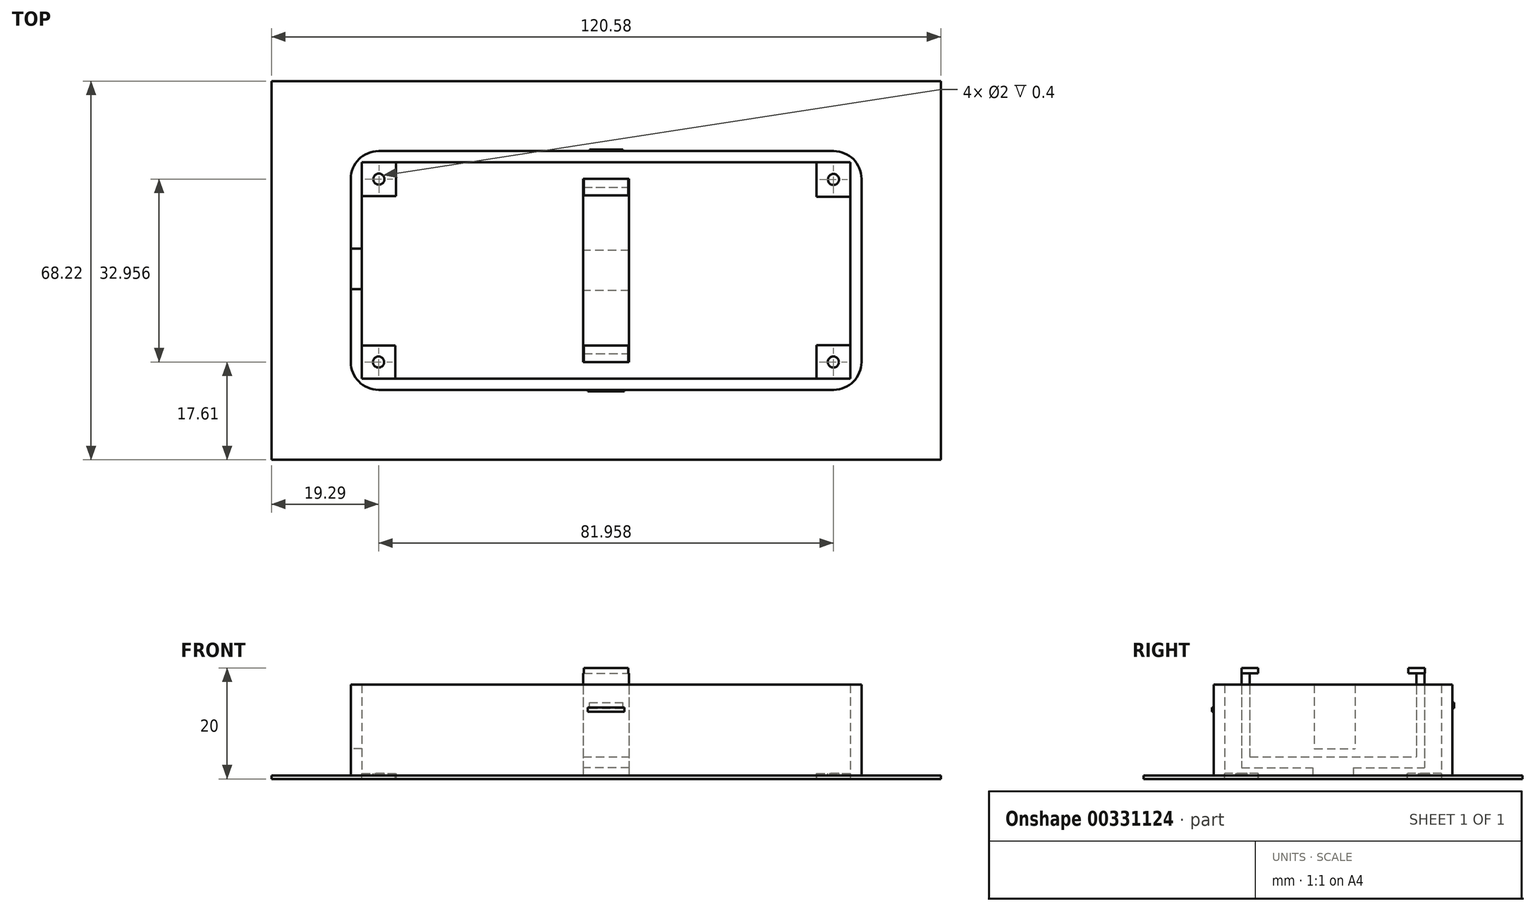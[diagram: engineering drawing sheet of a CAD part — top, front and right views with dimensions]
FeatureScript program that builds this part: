
annotation { "Feature Type Name" : "Feature", "Feature Type Description" : "" }
export const myFeature = defineFeature(function(context is Context, id is Id, definition is map)
    precondition{}
    {
        {
            var Q0;
            Q0=qCreatedBy(makeId("Top.planeOp"),FACE);
            var sketch = newSketch(context, id + "F0", { "sketchPlane" : qUnion([Q0])});
            skLineSegment(sketch, "E0.bottom", {"start": v(-46, 21.5) * mm, "end": v(46, 21.5) * mm});
            skLineSegment(sketch, "E0.top", {"start": v(-46, -21.5) * mm, "end": v(46, -21.5) * mm});
            skLineSegment(sketch, "E0.left", {"start": v(-46, 21.5) * mm, "end": v(-46, -21.5) * mm});
            skLineSegment(sketch, "E0.right", {"start": v(46, 21.5) * mm, "end": v(46, -21.5) * mm});
            skPoint(sketch, "E0.middle", {"position": v(0, 0) * mm});
            skLineSegment(sketch, "E1.bottom", {"start": v(-44, 19.5) * mm, "end": v(44, 19.5) * mm});
            skLineSegment(sketch, "E1.top", {"start": v(-44, -19.5) * mm, "end": v(44, -19.5) * mm});
            skLineSegment(sketch, "E1.left", {"start": v(-44, 19.5) * mm, "end": v(-44, -19.5) * mm});
            skLineSegment(sketch, "E1.right", {"start": v(44, 19.5) * mm, "end": v(44, -19.5) * mm});
            skLineSegment(sketch, "E2.bottom", {"start": v(-4.12, 19.5) * mm, "end": v(4.12, 19.5) * mm});
            skLineSegment(sketch, "E2.top", {"start": v(-4.12, -19.5) * mm, "end": v(4.12, -19.5) * mm});
            skLineSegment(sketch, "E2.left", {"start": v(-4.12, 19.5) * mm, "end": v(-4.12, -19.5) * mm});
            skLineSegment(sketch, "E2.right", {"start": v(4.12, 19.5) * mm, "end": v(4.12, -19.5) * mm});
            skLineSegment(sketch, "E3.bottom", {"start": v(44, 3.63) * mm, "end": v(-44, 3.63) * mm});
            skLineSegment(sketch, "E3.top", {"start": v(44, -3.63) * mm, "end": v(-44, -3.63) * mm});
            skLineSegment(sketch, "E3.left", {"start": v(44, 3.63) * mm, "end": v(44, -3.63) * mm});
            skLineSegment(sketch, "E3.right", {"start": v(-44, 3.63) * mm, "end": v(-44, -3.63) * mm});
            skSolve(sketch);
        }
        {
            var Q0;
            {var subQ5=sQuery(id+"F0.wireOp",EDGE,"E3.right");Q0=makeQuery(id+"F0.imprint","IMPRINT",FACE,{"disambiguationData":[TD([[makeQuery(id+"F0.imprint","IMPRINT",EDGE,{"derivedFrom":subQ5}),1.0]])]});}
            var Q1;
            {var subQ5=sQuery(id+"F0.wireOp",EDGE,"E3.left");Q1=makeQuery(id+"F0.imprint","IMPRINT",FACE,{"disambiguationData":[TD([[makeQuery(id+"F0.imprint","IMPRINT",EDGE,{"derivedFrom":subQ5}),-1.0]])]});}
            var Q2;
            {var subQ0=sQuery(id+"F0.wireOp",EDGE,"E2.top");Q2=makeQuery(id+"F0.imprint","IMPRINT",FACE,{"disambiguationData":[TD([[makeQuery(id+"F0.imprint","IMPRINT",EDGE,{"derivedFrom":subQ0}),1.0]])]});}
            var Q3;
            {var subQ0=sQuery(id+"F0.wireOp",EDGE,"E3.bottom");var subQ1=sQuery(id+"F0.wireOp",EDGE,"E2.left");var subQ2=makeQuery(id+"F0.imprint","INTERSECT",VERTEX,{"derivedFrom":[subQ1,subQ0]});Q3=makeQuery(id+"F0.imprint","IMPRINT",FACE,{"disambiguationData":[TD([[makeQuery(id+"F0.imprint","IMPRINT",EDGE,{"disambiguationData":[TD([[subQ2,-1.0]])],"derivedFrom":subQ1}),1.0]])]});}
            var Q4;
            {var subQ0=sQuery(id+"F0.wireOp",EDGE,"E2.bottom");Q4=makeQuery(id+"F0.imprint","IMPRINT",FACE,{"disambiguationData":[TD([[makeQuery(id+"F0.imprint","IMPRINT",EDGE,{"derivedFrom":subQ0}),-1.0]])]});}
            var Q5;
            Q5=makeQuery(id+"F0.imprint","IMPRINT",FACE,{"disambiguationData":[TD([[makeQuery(id+"F0.imprint","IMPRINT",EDGE,{"derivedFrom":sQuery(id+"F0.wireOp",EDGE,"E0.bottom")}),-1.0]])]});
            extrude(context, id + "F1", {"entities" : qUnion([Q0, Q1, Q2, Q3, Q4, Q5]), "depth" : 2 * mm});
        }
        {
            var Q0;
            Q0=makeQuery(id+"F1.opExtrude","CAP_FACE",FACE,{"disambiguationData":[OSD([sQuery(id+"F0.wireOp",EDGE,"E0.bottom"),sQuery(id+"F0.wireOp",EDGE,"E0.top"),sQuery(id+"F0.wireOp",EDGE,"E0.left"),sQuery(id+"F0.wireOp",EDGE,"E0.right"),sQuery(id+"F0.wireOp",EDGE,"E1.bottom"),sQuery(id+"F0.wireOp",EDGE,"E1.top"),sQuery(id+"F0.wireOp",EDGE,"E1.left"),sQuery(id+"F0.wireOp",EDGE,"E1.right"),sQuery(id+"F0.wireOp",EDGE,"E2.left"),sQuery(id+"F0.wireOp",EDGE,"E2.right"),sQuery(id+"F0.wireOp",EDGE,"E3.bottom"),sQuery(id+"F0.wireOp",EDGE,"E3.top")])],"isStart":false});
            var sketch = newSketch(context, id + "F2", { "sketchPlane" : qUnion([Q0])});
            skLineSegment(sketch, "E4.bottom", {"start": v(-4.12, 15) * mm, "end": v(4.12, 15) * mm});
            skLineSegment(sketch, "E4.top", {"start": v(-4.12, 16.5) * mm, "end": v(4.12, 16.5) * mm});
            skLineSegment(sketch, "E4.left", {"start": v(-4.12, 15) * mm, "end": v(-4.12, 16.5) * mm});
            skLineSegment(sketch, "E4.right", {"start": v(4.12, 15) * mm, "end": v(4.12, 16.5) * mm});
            skPoint(sketch, "E4.middle", {"position": v(0, 15.75) * mm});
            skLineSegment(sketch, "E5.bottom", {"start": v(-4.12, -15) * mm, "end": v(4.12, -15) * mm});
            skLineSegment(sketch, "E5.top", {"start": v(-4.12, -16.5) * mm, "end": v(4.12, -16.5) * mm});
            skLineSegment(sketch, "E5.left", {"start": v(-4.12, -15) * mm, "end": v(-4.12, -16.5) * mm});
            skLineSegment(sketch, "E5.right", {"start": v(4.12, -15) * mm, "end": v(4.12, -16.5) * mm});
            skPoint(sketch, "E5.middle", {"position": v(0, -15.75) * mm});
            skSolve(sketch);
        }
        {
            var Q0;
            Q0=makeQuery(id+"F2.imprint","IMPRINT",FACE,{"disambiguationData":[TD([[makeQuery(id+"F2.imprint","IMPRINT",EDGE,{"derivedFrom":sQuery(id+"F2.wireOp",EDGE,"E4.bottom")}),1.0]])]});
            extrude(context, id + "F3", {"entities" : qUnion([Q0]), "operationType" : NewBodyOperationType.ADD, "depth" : 17 * mm});
        }
        {
            var Q0;
            Q0=makeQuery(id+"F2.imprint","IMPRINT",FACE,{"disambiguationData":[TD([[makeQuery(id+"F2.imprint","IMPRINT",EDGE,{"derivedFrom":sQuery(id+"F2.wireOp",EDGE,"E5.bottom")}),-1.0]])]});
            extrude(context, id + "F4", {"entities" : qUnion([Q0]), "operationType" : NewBodyOperationType.ADD, "depth" : 17 * mm});
        }
        {
            var Q0;
            Q0=makeQuery(id+"F1.opExtrude","CAP_FACE",FACE,{"disambiguationData":[OSD([sQuery(id+"F0.wireOp",EDGE,"E0.bottom"),sQuery(id+"F0.wireOp",EDGE,"E0.top"),sQuery(id+"F0.wireOp",EDGE,"E0.left"),sQuery(id+"F0.wireOp",EDGE,"E0.right"),sQuery(id+"F0.wireOp",EDGE,"E1.bottom"),sQuery(id+"F0.wireOp",EDGE,"E1.top"),sQuery(id+"F0.wireOp",EDGE,"E1.left"),sQuery(id+"F0.wireOp",EDGE,"E1.right"),sQuery(id+"F0.wireOp",EDGE,"E2.left"),sQuery(id+"F0.wireOp",EDGE,"E2.right"),sQuery(id+"F0.wireOp",EDGE,"E3.bottom"),sQuery(id+"F0.wireOp",EDGE,"E3.top")])],"isStart":false});
            var sketch = newSketch(context, id + "F5", { "sketchPlane" : qUnion([Q0])});
            skLineSegment(sketch, "E6.bottom", {"start": v(-4.12, -15) * mm, "end": v(4.12, -15) * mm});
            skLineSegment(sketch, "E6.top", {"start": v(-4.12, 15) * mm, "end": v(4.12, 15) * mm});
            skLineSegment(sketch, "E6.left", {"start": v(-4.12, -15) * mm, "end": v(-4.12, 15) * mm});
            skLineSegment(sketch, "E6.right", {"start": v(4.12, -15) * mm, "end": v(4.12, 15) * mm});
            skPoint(sketch, "E6.middle", {"position": v(0, 0) * mm});
            skSolve(sketch);
        }
        {
            var Q0;
            {var subQ9=sQuery(id+"F5.wireOp",EDGE,"E6.bottom");Q0=makeQuery(id+"F5.imprint","IMPRINT",FACE,{"disambiguationData":[TD([[makeQuery(id+"F5.imprint","IMPRINT",EDGE,{"derivedFrom":subQ9}),1.0]])]});}
            extrude(context, id + "F6", {"entities" : qUnion([Q0]), "operationType" : NewBodyOperationType.ADD, "depth" : 2 * mm});
        }
        {
            var Q0;
            Q0=makeQuery(id+"F4.opExtrude","CAP_FACE",FACE,{"disambiguationData":[OSD([sQuery(id+"F2.wireOp",EDGE,"E5.bottom"),sQuery(id+"F2.wireOp",EDGE,"E5.top"),sQuery(id+"F2.wireOp",EDGE,"E5.left"),sQuery(id+"F2.wireOp",EDGE,"E5.right")])],"isStart":false});
            var sketch = newSketch(context, id + "F7", { "sketchPlane" : qUnion([Q0])});
            skLineSegment(sketch, "E7.bottom", {"start": v(-4, -13.5) * mm, "end": v(4, -13.5) * mm});
            skLineSegment(sketch, "E7.top", {"start": v(-4, -16.5) * mm, "end": v(4, -16.5) * mm});
            skLineSegment(sketch, "E7.left", {"start": v(-4, -13.5) * mm, "end": v(-4, -16.5) * mm});
            skLineSegment(sketch, "E7.right", {"start": v(4, -13.5) * mm, "end": v(4, -16.5) * mm});
            skPoint(sketch, "E7.middle", {"position": v(0, -15) * mm});
            skLineSegment(sketch, "E8.bottom", {"start": v(-4, 13.54) * mm, "end": v(4, 13.54) * mm});
            skLineSegment(sketch, "E8.top", {"start": v(-4, 16.54) * mm, "end": v(4, 16.54) * mm});
            skLineSegment(sketch, "E8.left", {"start": v(-4, 13.54) * mm, "end": v(-4, 16.54) * mm});
            skLineSegment(sketch, "E8.right", {"start": v(4, 13.54) * mm, "end": v(4, 16.54) * mm});
            skPoint(sketch, "E8.middle", {"position": v(0, 15.04) * mm});
            skSolve(sketch);
        }
        {
            var Q0;
            Q0 = qSketchRegion(id + "F7", true);
            extrude(context, id + "F8", {"entities" : qUnion([Q0]), "operationType" : NewBodyOperationType.ADD, "depth" : 1 * mm});
        }
        {
            var Q0;
            Q0=qCreatedBy(makeId("Top.planeOp"),FACE);
            var sketch = newSketch(context, id + "F9", { "sketchPlane" : qUnion([Q0])});
            skLineSegment(sketch, "E9.bottom", {"start": v(-46, -21.5) * mm, "end": v(-38, -21.5) * mm});
            skLineSegment(sketch, "E9.top", {"start": v(-46, -13.5) * mm, "end": v(-38, -13.5) * mm});
            skLineSegment(sketch, "E9.left", {"start": v(-46, -21.5) * mm, "end": v(-46, -13.5) * mm});
            skLineSegment(sketch, "E9.right", {"start": v(-38, -21.5) * mm, "end": v(-38, -13.5) * mm});
            skSolve(sketch);
        }
        {
            var Q0;
            Q0=qCreatedBy(makeId("Top.planeOp"),FACE);
            var sketch = newSketch(context, id + "F10", { "sketchPlane" : qUnion([Q0])});
            skLineSegment(sketch, "E10.bottom", {"start": v(-45.88, 21.41) * mm, "end": v(-37.88, 21.41) * mm});
            skLineSegment(sketch, "E10.top", {"start": v(-45.88, 13.41) * mm, "end": v(-37.88, 13.41) * mm});
            skLineSegment(sketch, "E10.left", {"start": v(-45.88, 21.41) * mm, "end": v(-45.88, 13.41) * mm});
            skLineSegment(sketch, "E10.right", {"start": v(-37.88, 21.41) * mm, "end": v(-37.88, 13.41) * mm});
            skSolve(sketch);
        }
        {
            var Q0;
            Q0 = qSketchRegion(id + "F10", true);
            extrude(context, id + "F11", {"entities" : qUnion([Q0]), "operationType" : NewBodyOperationType.ADD, "depth" : 1 * mm});
        }
        {
            var Q0;
            Q0 = qSketchRegion(id + "F9", true);
            extrude(context, id + "F12", {"entities" : qUnion([Q0]), "operationType" : NewBodyOperationType.ADD, "depth" : 1 * mm});
        }
        {
            var Q0;
            Q0=qCreatedBy(makeId("Top.planeOp"),FACE);
            var sketch = newSketch(context, id + "F13", { "sketchPlane" : qUnion([Q0])});
            skLineSegment(sketch, "E11.bottom", {"start": v(45.92, 21.28) * mm, "end": v(37.92, 21.28) * mm});
            skLineSegment(sketch, "E11.top", {"start": v(45.92, 13.28) * mm, "end": v(37.92, 13.28) * mm});
            skLineSegment(sketch, "E11.left", {"start": v(45.92, 21.28) * mm, "end": v(45.92, 13.28) * mm});
            skLineSegment(sketch, "E11.right", {"start": v(37.92, 21.28) * mm, "end": v(37.92, 13.28) * mm});
            skSolve(sketch);
        }
        {
            var Q0;
            Q0 = qSketchRegion(id + "F13", true);
            extrude(context, id + "F14", {"entities" : qUnion([Q0]), "operationType" : NewBodyOperationType.ADD, "depth" : 1 * mm});
        }
        {
            var Q0;
            Q0=qCreatedBy(makeId("Top.planeOp"),FACE);
            var sketch = newSketch(context, id + "F15", { "sketchPlane" : qUnion([Q0])});
            skLineSegment(sketch, "E12.bottom", {"start": v(45.87, -21.5) * mm, "end": v(37.87, -21.5) * mm});
            skLineSegment(sketch, "E12.top", {"start": v(45.87, -13.5) * mm, "end": v(37.87, -13.5) * mm});
            skLineSegment(sketch, "E12.left", {"start": v(45.87, -21.5) * mm, "end": v(45.87, -13.5) * mm});
            skLineSegment(sketch, "E12.right", {"start": v(37.87, -21.5) * mm, "end": v(37.87, -13.5) * mm});
            skSolve(sketch);
        }
        {
            var Q0;
            Q0 = qSketchRegion(id + "F15", true);
            extrude(context, id + "F16", {"entities" : qUnion([Q0]), "operationType" : NewBodyOperationType.ADD, "depth" : 1 * mm});
        }
        {
            var Q0;
            Q0=makeQuery(id+"F1.opExtrude","CAP_FACE",FACE,{"disambiguationData":[OSD([sQuery(id+"F0.wireOp",EDGE,"E0.bottom"),sQuery(id+"F0.wireOp",EDGE,"E0.top"),sQuery(id+"F0.wireOp",EDGE,"E0.left"),sQuery(id+"F0.wireOp",EDGE,"E0.right"),sQuery(id+"F0.wireOp",EDGE,"E1.bottom"),sQuery(id+"F0.wireOp",EDGE,"E1.top"),sQuery(id+"F0.wireOp",EDGE,"E1.left"),sQuery(id+"F0.wireOp",EDGE,"E1.right"),sQuery(id+"F0.wireOp",EDGE,"E2.left"),sQuery(id+"F0.wireOp",EDGE,"E2.right"),sQuery(id+"F0.wireOp",EDGE,"E3.bottom"),sQuery(id+"F0.wireOp",EDGE,"E3.top")])],"isStart":false});
            var sketch = newSketch(context, id + "F17", { "sketchPlane" : qUnion([Q0])});
            skLineSegment(sketch, "E13", {"start": v(-4.12, -19.5) * mm, "end": v(4.12, -19.5) * mm});
            skLineSegment(sketch, "E14", {"start": v(-4.12, 19.5) * mm, "end": v(4.12, 19.5) * mm});
            skLineSegment(sketch, "E15", {"start": v(44, -3.63) * mm, "end": v(44, 3.63) * mm});
            skLineSegment(sketch, "E16", {"start": v(-44, -3.63) * mm, "end": v(-44, 3.63) * mm});
            skSolve(sketch);
        }
        {
            var Q0;
            Q0=makeQuery(id+"F17.imprint","IMPRINT",FACE,{"disambiguationData":[TD([[makeQuery(id+"F17.imprint","IMPRINT",EDGE,{"derivedFrom":sQuery(id+"F17.wireOp",EDGE,"E13")}),-1.0]])]});
            extrude(context, id + "F18", {"entities" : qUnion([Q0]), "operationType" : NewBodyOperationType.ADD, "depth" : 15 * mm});
        }
        {
            var Q0;
            Q0=makeQuery(id+"F12.opExtrude","CAP_FACE",FACE,{"disambiguationData":[OSD([sQuery(id+"F9.wireOp",EDGE,"E9.bottom"),sQuery(id+"F9.wireOp",EDGE,"E9.top"),sQuery(id+"F9.wireOp",EDGE,"E9.left"),sQuery(id+"F9.wireOp",EDGE,"E9.right")])],"isStart":false});
            var sketch = newSketch(context, id + "F19", { "sketchPlane" : qUnion([Q0])});
            skCircle(sketch, "E17", {"center": v(-41, -16.5) * mm, "radius": 3 * mm});
            skPoint(sketch, "E17.centerSnap0", {"position": v(-44, -16.5) * mm});
            skPoint(sketch, "E17.centerSnap1", {"position": v(-41, -19.5) * mm});
            skSolve(sketch);
        }
        {
            var Q0;
            Q0=sQuery(id+"F19.wireOp",VERTEX,"E17.center");
            var Q1;
            Q1=makeQuery(id+"F1.opExtrude","SWEPT_BODY",BODY,{"disambiguationData":[OSD([sQuery(id+"F0.wireOp",EDGE,"E0.bottom"),sQuery(id+"F0.wireOp",EDGE,"E0.top"),sQuery(id+"F0.wireOp",EDGE,"E0.left"),sQuery(id+"F0.wireOp",EDGE,"E0.right"),sQuery(id+"F0.wireOp",EDGE,"E1.bottom"),sQuery(id+"F0.wireOp",EDGE,"E1.top"),sQuery(id+"F0.wireOp",EDGE,"E1.left"),sQuery(id+"F0.wireOp",EDGE,"E1.right"),sQuery(id+"F0.wireOp",EDGE,"E2.left"),sQuery(id+"F0.wireOp",EDGE,"E2.right"),sQuery(id+"F0.wireOp",EDGE,"E3.bottom"),sQuery(id+"F0.wireOp",EDGE,"E3.top")])]});
            hole(context, id + "F20", {"style" : HoleStyle.SIMPLE, "endStyle" : HoleEndStyle.BLIND, "holeDiameter" : 2 * mm, "holeDepth" : 12 * mm, "tappedDepth" : 12 * mm, "tapClearance" : 3, "startFromSketch" : true, "locations" : qUnion([Q0]), "scope" : qUnion([Q1])});
        }
        {
            var Q0;
            Q0=makeQuery(id+"F11.opExtrude","CAP_FACE",FACE,{"disambiguationData":[OSD([sQuery(id+"F10.wireOp",EDGE,"E10.bottom"),sQuery(id+"F10.wireOp",EDGE,"E10.top"),sQuery(id+"F10.wireOp",EDGE,"E10.left"),sQuery(id+"F10.wireOp",EDGE,"E10.right")])],"isStart":false});
            var sketch = newSketch(context, id + "F21", { "sketchPlane" : qUnion([Q0])});
            skCircle(sketch, "E18", {"center": v(-40.94, 16.46) * mm, "radius": 3.04 * mm});
            skPoint(sketch, "E18.centerSnap0", {"position": v(-40.94, 19.5) * mm});
            skPoint(sketch, "E18.centerSnap1", {"position": v(-44, 16.46) * mm});
            skSolve(sketch);
        }
        {
            var Q0;
            Q0=sQuery(id+"F21.wireOp",VERTEX,"E18.center");
            var Q1;
            Q1=makeQuery(id+"F1.opExtrude","SWEPT_BODY",BODY,{"disambiguationData":[OSD([sQuery(id+"F0.wireOp",EDGE,"E0.bottom"),sQuery(id+"F0.wireOp",EDGE,"E0.top"),sQuery(id+"F0.wireOp",EDGE,"E0.left"),sQuery(id+"F0.wireOp",EDGE,"E0.right"),sQuery(id+"F0.wireOp",EDGE,"E1.bottom"),sQuery(id+"F0.wireOp",EDGE,"E1.top"),sQuery(id+"F0.wireOp",EDGE,"E1.left"),sQuery(id+"F0.wireOp",EDGE,"E1.right"),sQuery(id+"F0.wireOp",EDGE,"E2.left"),sQuery(id+"F0.wireOp",EDGE,"E2.right"),sQuery(id+"F0.wireOp",EDGE,"E3.bottom"),sQuery(id+"F0.wireOp",EDGE,"E3.top")])]});
            hole(context, id + "F22", {"style" : HoleStyle.SIMPLE, "endStyle" : HoleEndStyle.BLIND, "holeDiameter" : 2 * mm, "holeDepth" : 12 * mm, "tappedDepth" : 12 * mm, "tapClearance" : 3, "startFromSketch" : true, "locations" : qUnion([Q0]), "scope" : qUnion([Q1])});
        }
        {
            var Q0;
            Q0=makeQuery(id+"F14.opExtrude","CAP_FACE",FACE,{"disambiguationData":[OSD([sQuery(id+"F13.wireOp",EDGE,"E11.bottom"),sQuery(id+"F13.wireOp",EDGE,"E11.top"),sQuery(id+"F13.wireOp",EDGE,"E11.left"),sQuery(id+"F13.wireOp",EDGE,"E11.right")])],"isStart":false});
            var sketch = newSketch(context, id + "F23", { "sketchPlane" : qUnion([Q0])});
            skCircle(sketch, "E19", {"center": v(40.96, 16.4) * mm, "radius": 2.25 * mm});
            skPoint(sketch, "E19.centerSnap0", {"position": v(44, 16.4) * mm});
            skPoint(sketch, "E19.centerSnap1", {"position": v(40.96, 13.28) * mm});
            skSolve(sketch);
        }
        {
            var Q0;
            Q0=sQuery(id+"F23.wireOp",VERTEX,"E19.center");
            var Q1;
            Q1=makeQuery(id+"F1.opExtrude","SWEPT_BODY",BODY,{"disambiguationData":[OSD([sQuery(id+"F0.wireOp",EDGE,"E0.bottom"),sQuery(id+"F0.wireOp",EDGE,"E0.top"),sQuery(id+"F0.wireOp",EDGE,"E0.left"),sQuery(id+"F0.wireOp",EDGE,"E0.right"),sQuery(id+"F0.wireOp",EDGE,"E1.bottom"),sQuery(id+"F0.wireOp",EDGE,"E1.top"),sQuery(id+"F0.wireOp",EDGE,"E1.left"),sQuery(id+"F0.wireOp",EDGE,"E1.right"),sQuery(id+"F0.wireOp",EDGE,"E2.left"),sQuery(id+"F0.wireOp",EDGE,"E2.right"),sQuery(id+"F0.wireOp",EDGE,"E3.bottom"),sQuery(id+"F0.wireOp",EDGE,"E3.top")])]});
            hole(context, id + "F24", {"style" : HoleStyle.SIMPLE, "endStyle" : HoleEndStyle.BLIND, "holeDiameter" : 2 * mm, "holeDepth" : 12 * mm, "tappedDepth" : 12 * mm, "tapClearance" : 3, "startFromSketch" : true, "locations" : qUnion([Q0]), "scope" : qUnion([Q1])});
        }
        {
            var Q0;
            Q0=makeQuery(id+"F16.opExtrude","CAP_FACE",FACE,{"disambiguationData":[OSD([sQuery(id+"F15.wireOp",EDGE,"E12.bottom"),sQuery(id+"F15.wireOp",EDGE,"E12.top"),sQuery(id+"F15.wireOp",EDGE,"E12.left"),sQuery(id+"F15.wireOp",EDGE,"E12.right")])],"isStart":false});
            var sketch = newSketch(context, id + "F25", { "sketchPlane" : qUnion([Q0])});
            skCircle(sketch, "E20", {"center": v(40.94, -16.5) * mm, "radius": 2.86 * mm});
            skPoint(sketch, "E20.centerSnap0", {"position": v(44, -16.5) * mm});
            skPoint(sketch, "E20.centerSnap1", {"position": v(40.94, -19.5) * mm});
            skSolve(sketch);
        }
        {
            var Q0;
            Q0=sQuery(id+"F25.wireOp",VERTEX,"E20.center");
            var Q1;
            Q1=makeQuery(id+"F1.opExtrude","SWEPT_BODY",BODY,{"disambiguationData":[OSD([sQuery(id+"F0.wireOp",EDGE,"E0.bottom"),sQuery(id+"F0.wireOp",EDGE,"E0.top"),sQuery(id+"F0.wireOp",EDGE,"E0.left"),sQuery(id+"F0.wireOp",EDGE,"E0.right"),sQuery(id+"F0.wireOp",EDGE,"E1.bottom"),sQuery(id+"F0.wireOp",EDGE,"E1.top"),sQuery(id+"F0.wireOp",EDGE,"E1.left"),sQuery(id+"F0.wireOp",EDGE,"E1.right"),sQuery(id+"F0.wireOp",EDGE,"E2.left"),sQuery(id+"F0.wireOp",EDGE,"E2.right"),sQuery(id+"F0.wireOp",EDGE,"E3.bottom"),sQuery(id+"F0.wireOp",EDGE,"E3.top")])]});
            hole(context, id + "F26", {"style" : HoleStyle.SIMPLE, "endStyle" : HoleEndStyle.BLIND, "holeDiameter" : 2 * mm, "holeDepth" : 12 * mm, "tappedDepth" : 12 * mm, "tapClearance" : 3, "startFromSketch" : true, "locations" : qUnion([Q0]), "scope" : qUnion([Q1])});
        }
        {
            var Q0;
            {var subQ0=sQuery(id+"F0.wireOp",EDGE,"E0.left");Q0=makeQuery(id+"F18.boolean.opBoolean","MERGE",FACE,{"derivedFrom":[makeQuery(id+"F1.opExtrude","SWEPT_FACE",FACE,{"disambiguationData":[OSD([subQ0])]}),makeQuery(id+"F18.opExtrude","SWEPT_FACE",FACE,{"disambiguationData":[OSD([subQ0])]})]});}
            var sketch = newSketch(context, id + "F27", { "sketchPlane" : qUnion([Q0])});
            skLineSegment(sketch, "E21.bottom", {"start": v(-3.96, 5.41) * mm, "end": v(3.38, 5.41) * mm});
            skLineSegment(sketch, "E21.top", {"start": v(-3.96, 17) * mm, "end": v(3.38, 17) * mm});
            skLineSegment(sketch, "E21.left", {"start": v(-3.96, 5.41) * mm, "end": v(-3.96, 17) * mm});
            skLineSegment(sketch, "E21.right", {"start": v(3.38, 5.41) * mm, "end": v(3.38, 17) * mm});
            skSolve(sketch);
        }
        {
            var Q0;
            Q0=makeQuery(id+"F27.imprint","IMPRINT",FACE,{"disambiguationData":[TD([[makeQuery(id+"F27.imprint","IMPRINT",EDGE,{"derivedFrom":sQuery(id+"F27.wireOp",EDGE,"E21.bottom")}),1.0]])]});
            extrude(context, id + "F28", {"entities" : qUnion([Q0]), "operationType" : NewBodyOperationType.REMOVE, "oppositeDirection" : true, "depth" : 3 * mm});
        }
        {
            var Q0;
            {var subQ0=sQuery(id+"F0.wireOp",EDGE,"E0.top");Q0=makeQuery(id+"F18.boolean.opBoolean","MERGE",FACE,{"derivedFrom":[makeQuery(id+"F1.opExtrude","SWEPT_FACE",FACE,{"disambiguationData":[OSD([subQ0])]}),makeQuery(id+"F18.opExtrude","SWEPT_FACE",FACE,{"disambiguationData":[OSD([subQ0])]})]});}
            var sketch = newSketch(context, id + "F29", { "sketchPlane" : qUnion([Q0])});
            skLineSegment(sketch, "E22.bottom", {"start": v(3.29, 12.08) * mm, "end": v(-3.29, 12.08) * mm});
            skLineSegment(sketch, "E22.top", {"start": v(3.29, 12.85) * mm, "end": v(-3.29, 12.85) * mm});
            skLineSegment(sketch, "E22.left", {"start": v(3.29, 12.08) * mm, "end": v(3.29, 12.85) * mm});
            skLineSegment(sketch, "E22.right", {"start": v(-3.29, 12.08) * mm, "end": v(-3.29, 12.85) * mm});
            skPoint(sketch, "E22.middle", {"position": v(0, 12.46) * mm});
            skSolve(sketch);
        }
        {
            var Q0;
            Q0 = qSketchRegion(id + "F29", true);
            extrude(context, id + "F30", {"entities" : qUnion([Q0]), "operationType" : NewBodyOperationType.ADD, "depth" : .3 * mm});
        }
        {
            var Q0;
            {var subQ0=sQuery(id+"F0.wireOp",EDGE,"E0.bottom");Q0=makeQuery(id+"F18.boolean.opBoolean","MERGE",FACE,{"derivedFrom":[makeQuery(id+"F1.opExtrude","SWEPT_FACE",FACE,{"disambiguationData":[OSD([subQ0])]}),makeQuery(id+"F18.opExtrude","SWEPT_FACE",FACE,{"disambiguationData":[OSD([subQ0])]})]});}
            var sketch = newSketch(context, id + "F31", { "sketchPlane" : qUnion([Q0])});
            skLineSegment(sketch, "E23.bottom", {"start": v(3.02, 12.74) * mm, "end": v(-3.02, 12.74) * mm});
            skLineSegment(sketch, "E23.top", {"start": v(3.02, 13.73) * mm, "end": v(-3.02, 13.73) * mm});
            skLineSegment(sketch, "E23.left", {"start": v(3.02, 12.74) * mm, "end": v(3.02, 13.73) * mm});
            skLineSegment(sketch, "E23.right", {"start": v(-3.02, 12.74) * mm, "end": v(-3.02, 13.73) * mm});
            skPoint(sketch, "E23.middle", {"position": v(0, 13.24) * mm});
            skSolve(sketch);
        }
        {
            var Q0;
            Q0=makeQuery(id+"F31.imprint","IMPRINT",FACE,{"disambiguationData":[TD([[makeQuery(id+"F31.imprint","IMPRINT",EDGE,{"derivedFrom":sQuery(id+"F31.wireOp",EDGE,"E23.bottom")}),-1.0]])]});
            extrude(context, id + "F32", {"entities" : qUnion([Q0]), "operationType" : NewBodyOperationType.ADD, "depth" : .3 * mm});
        }
        {
            var Q0;
            {var subQ0=sQuery(id+"F0.wireOp",EDGE,"E0.left");var subQ1=sQuery(id+"F0.wireOp",EDGE,"E0.top");Q0=makeQuery(id+"F18.boolean.opBoolean","MERGE",EDGE,{"derivedFrom":[makeQuery(id+"F1.opExtrude","SWEPT_EDGE",EDGE,{"disambiguationData":[OSD([subQ1,subQ0])]}),makeQuery(id+"F18.opExtrude","SWEPT_EDGE",EDGE,{"disambiguationData":[OSD([subQ1,subQ0])]})]});}
            fillet(context, id + "F33", {"entities" : qUnion([Q0]), "radius" : 5 * mm, "tangentPropagation" : true, "allowEdgeOverflow" : false});
        }
        {
            var Q0;
            {var subQ0=sQuery(id+"F0.wireOp",EDGE,"E0.right");var subQ1=sQuery(id+"F0.wireOp",EDGE,"E0.top");Q0=makeQuery(id+"F18.boolean.opBoolean","MERGE",EDGE,{"derivedFrom":[makeQuery(id+"F1.opExtrude","SWEPT_EDGE",EDGE,{"disambiguationData":[OSD([subQ1,subQ0])]}),makeQuery(id+"F18.opExtrude","SWEPT_EDGE",EDGE,{"disambiguationData":[OSD([subQ1,subQ0])]})]});}
            fillet(context, id + "F34", {"entities" : qUnion([Q0]), "radius" : 5 * mm, "tangentPropagation" : true, "allowEdgeOverflow" : false});
        }
        {
            var Q0;
            {var subQ0=sQuery(id+"F0.wireOp",EDGE,"E0.right");var subQ1=sQuery(id+"F0.wireOp",EDGE,"E0.bottom");Q0=makeQuery(id+"F18.boolean.opBoolean","MERGE",EDGE,{"derivedFrom":[makeQuery(id+"F1.opExtrude","SWEPT_EDGE",EDGE,{"disambiguationData":[OSD([subQ1,subQ0])]}),makeQuery(id+"F18.opExtrude","SWEPT_EDGE",EDGE,{"disambiguationData":[OSD([subQ1,subQ0])]})]});}
            fillet(context, id + "F35", {"entities" : qUnion([Q0]), "radius" : 5 * mm, "tangentPropagation" : true, "allowEdgeOverflow" : false});
        }
        {
            var Q0;
            {var subQ0=sQuery(id+"F0.wireOp",EDGE,"E0.left");var subQ1=sQuery(id+"F0.wireOp",EDGE,"E0.bottom");Q0=makeQuery(id+"F18.boolean.opBoolean","MERGE",EDGE,{"derivedFrom":[makeQuery(id+"F1.opExtrude","SWEPT_EDGE",EDGE,{"disambiguationData":[OSD([subQ1,subQ0])]}),makeQuery(id+"F18.opExtrude","SWEPT_EDGE",EDGE,{"disambiguationData":[OSD([subQ1,subQ0])]})]});}
            fillet(context, id + "F36", {"entities" : qUnion([Q0]), "radius" : 5 * mm, "tangentPropagation" : true, "allowEdgeOverflow" : false});
        }
        {
            var Q0;
            Q0=qCreatedBy(makeId("Top.planeOp"),FACE);
            var sketch = newSketch(context, id + "F37", { "sketchPlane" : qUnion([Q0])});
            skLineSegment(sketch, "E24.bottom", {"start": v(-60.3, 34.1) * mm, "end": v(60.3, 34.1) * mm});
            skLineSegment(sketch, "E24.top", {"start": v(-60.3, -34.1) * mm, "end": v(60.3, -34.1) * mm});
            skLineSegment(sketch, "E24.left", {"start": v(-60.3, 34.1) * mm, "end": v(-60.3, -34.1) * mm});
            skLineSegment(sketch, "E24.right", {"start": v(60.3, 34.1) * mm, "end": v(60.3, -34.1) * mm});
            skPoint(sketch, "E24.middle", {"position": v(0, 0) * mm});
            skSolve(sketch);
        }
        {
            var Q0;
            Q0 = qSketchRegion(id + "F37", true);
            extrude(context, id + "F38", {"entities" : qUnion([Q0]), "operationType" : NewBodyOperationType.ADD, "depth" : .6 * mm});
        }
        {
            var Q0;
            Q0=makeQuery(id+"F38.boolean.opBoolean","SPLIT",FACE,{"disambiguationData":[TD([makeQuery(id+"F12.opExtrude","SWEPT_FACE",FACE,{"disambiguationData":[OSD([sQuery(id+"F9.wireOp",EDGE,"E9.top")])]})])],"derivedFrom":makeQuery(id+"F38.opExtrude","CAP_FACE",FACE,{"disambiguationData":[OSD([sQuery(id+"F37.wireOp",EDGE,"E24.bottom"),sQuery(id+"F37.wireOp",EDGE,"E24.top"),sQuery(id+"F37.wireOp",EDGE,"E24.left"),sQuery(id+"F37.wireOp",EDGE,"E24.right")])],"isStart":false})});
            var Q1;
            Q1=makeQuery(id+"F38.boolean.opBoolean","SPLIT",FACE,{"disambiguationData":[TD([makeQuery(id+"F11.opExtrude","SWEPT_FACE",FACE,{"disambiguationData":[OSD([sQuery(id+"F10.wireOp",EDGE,"E10.top")])]})])],"derivedFrom":makeQuery(id+"F38.opExtrude","CAP_FACE",FACE,{"disambiguationData":[OSD([sQuery(id+"F37.wireOp",EDGE,"E24.bottom"),sQuery(id+"F37.wireOp",EDGE,"E24.top"),sQuery(id+"F37.wireOp",EDGE,"E24.left"),sQuery(id+"F37.wireOp",EDGE,"E24.right")])],"isStart":false})});
            var Q2;
            Q2=makeQuery(id+"F38.boolean.opBoolean","SPLIT",FACE,{"disambiguationData":[TD([makeQuery(id+"F14.opExtrude","SWEPT_FACE",FACE,{"disambiguationData":[OSD([sQuery(id+"F13.wireOp",EDGE,"E11.top")])]})])],"derivedFrom":makeQuery(id+"F38.opExtrude","CAP_FACE",FACE,{"disambiguationData":[OSD([sQuery(id+"F37.wireOp",EDGE,"E24.bottom"),sQuery(id+"F37.wireOp",EDGE,"E24.top"),sQuery(id+"F37.wireOp",EDGE,"E24.left"),sQuery(id+"F37.wireOp",EDGE,"E24.right")])],"isStart":false})});
            var Q3;
            Q3=makeQuery(id+"F38.boolean.opBoolean","SPLIT",FACE,{"disambiguationData":[TD([makeQuery(id+"F16.opExtrude","SWEPT_FACE",FACE,{"disambiguationData":[OSD([sQuery(id+"F15.wireOp",EDGE,"E12.top")])]})])],"derivedFrom":makeQuery(id+"F38.opExtrude","CAP_FACE",FACE,{"disambiguationData":[OSD([sQuery(id+"F37.wireOp",EDGE,"E24.bottom"),sQuery(id+"F37.wireOp",EDGE,"E24.top"),sQuery(id+"F37.wireOp",EDGE,"E24.left"),sQuery(id+"F37.wireOp",EDGE,"E24.right")])],"isStart":false})});
            extrude(context, id + "F39", {"entities" : qUnion([Q0, Q1, Q2, Q3]), "operationType" : NewBodyOperationType.REMOVE, "oppositeDirection" : true, "depth" : 25 * mm});
        }
    });
